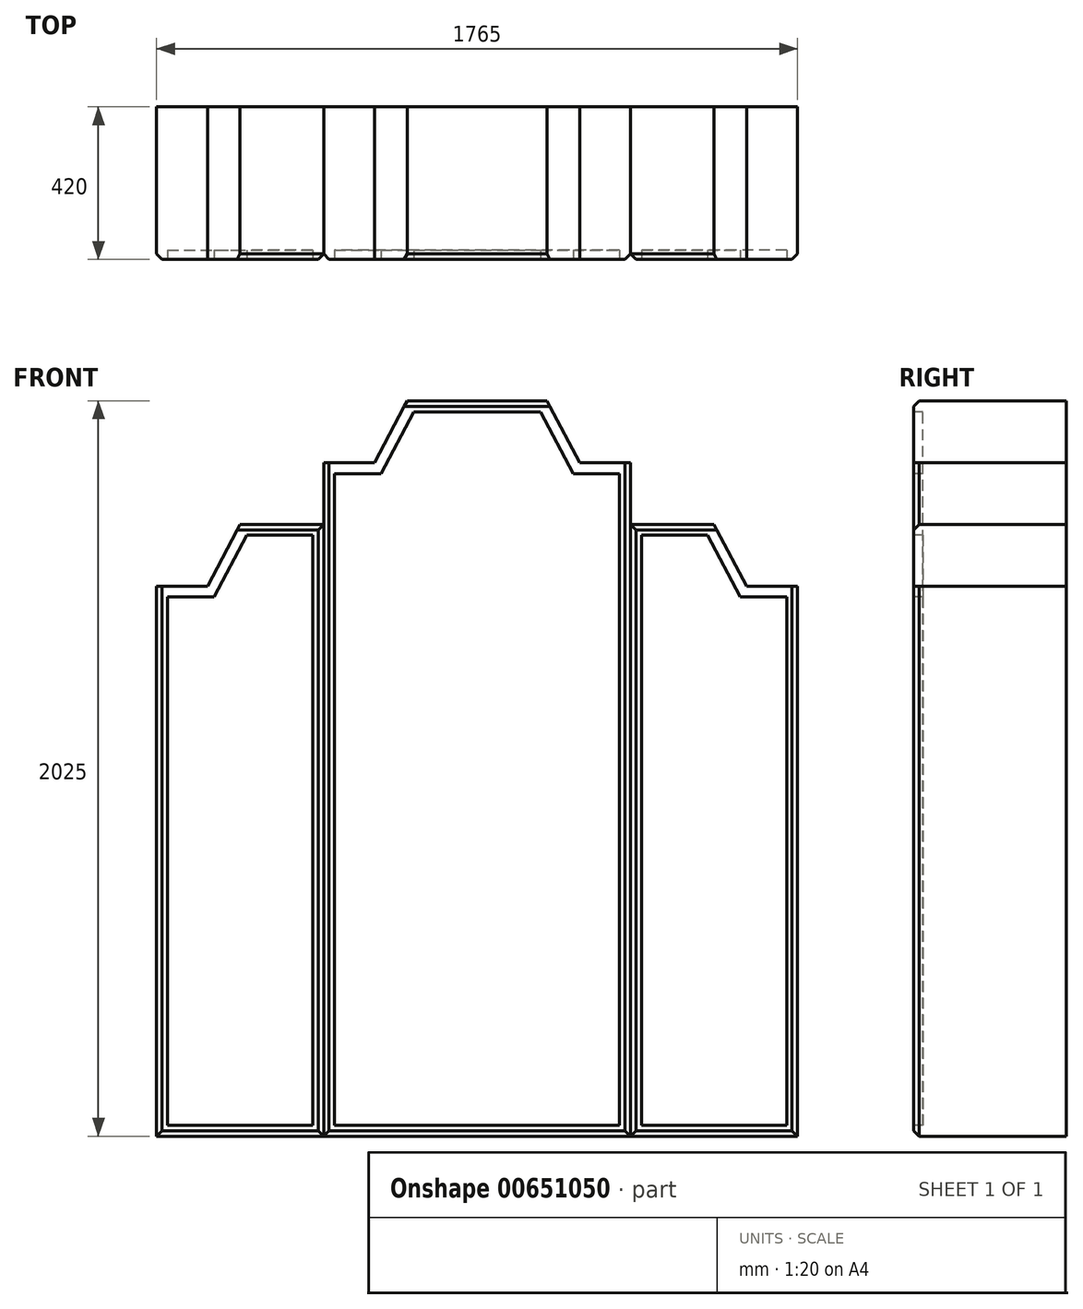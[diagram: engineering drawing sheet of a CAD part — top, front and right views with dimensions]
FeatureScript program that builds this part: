
annotation { "Feature Type Name" : "Feature", "Feature Type Description" : "" }
export const myFeature = defineFeature(function(context is Context, id is Id, definition is map)
    precondition{}
    {
        {
            var Q0;
            Q0=qCreatedBy(makeId("Top.planeOp"),FACE);
            var sketch = newSketch(context, id + "F0", { "sketchPlane" : qUnion([Q0])});
            skLineSegment(sketch, "E0.bottom", {"start": v(0, 0) * mm, "end": v(-460, 0) * mm});
            skLineSegment(sketch, "E0.top", {"start": v(0, 420) * mm, "end": v(-460, 420) * mm});
            skLineSegment(sketch, "E0.left", {"start": v(0, 0) * mm, "end": v(0, 420) * mm});
            skLineSegment(sketch, "E0.right", {"start": v(-460, 0) * mm, "end": v(-460, 420) * mm});
            skLineSegment(sketch, "E1.bottom", {"start": v(-460, 0) * mm, "end": v(-1305, 0) * mm});
            skLineSegment(sketch, "E1.top", {"start": v(-460, 420) * mm, "end": v(-1305, 420) * mm});
            skLineSegment(sketch, "E1.right", {"start": v(-1305, 0) * mm, "end": v(-1305, 420) * mm});
            skLineSegment(sketch, "E2.bottom", {"start": v(-1305, 0) * mm, "end": v(-1765, 0) * mm});
            skLineSegment(sketch, "E2.top", {"start": v(-1305, 420) * mm, "end": v(-1765, 420) * mm});
            skLineSegment(sketch, "E2.right", {"start": v(-1765, 0) * mm, "end": v(-1765, 420) * mm});
            skSolve(sketch);
        }
        {
            var Q0;
            Q0=makeQuery(id+"F0.imprint","IMPRINT",FACE,{"disambiguationData":[TD([[makeQuery(id+"F0.imprint","IMPRINT",EDGE,{"derivedFrom":sQuery(id+"F0.wireOp",EDGE,"E2.bottom")}),-1.0]])]});
            var Q1;
            Q1=makeQuery(id+"F0.imprint","IMPRINT",FACE,{"disambiguationData":[TD([[makeQuery(id+"F0.imprint","IMPRINT",EDGE,{"derivedFrom":sQuery(id+"F0.wireOp",EDGE,"E0.bottom")}),-1.0]])]});
            extrude(context, id + "F1", {"entities" : qUnion([Q0, Q1]), "depth" : 1685 * mm, "offsetDistance" : 25 * mm});
        }
        {
            var Q0;
            Q0=makeQuery(id+"F0.imprint","IMPRINT",FACE,{"disambiguationData":[TD([[makeQuery(id+"F0.imprint","IMPRINT",EDGE,{"derivedFrom":sQuery(id+"F0.wireOp",EDGE,"E1.bottom")}),-1.0]])]});
            extrude(context, id + "F2", {"entities" : qUnion([Q0]), "depth" : 2025 * mm, "offsetDistance" : 25 * mm});
        }
        {
            var Q0;
            Q0=makeQuery(id+"F1.opExtrude","SWEPT_FACE",FACE,{"disambiguationData":[OSD([sQuery(id+"F0.wireOp",EDGE,"E2.bottom")])]});
            var sketch = newSketch(context, id + "F3", { "sketchPlane" : qUnion([Q0])});
            skLineSegment(sketch, "E3.0.0", {"start": v(-1765, 0) * mm, "end": v(-1305, 0) * mm});
            skLineSegment(sketch, "E3.0.1", {"start": v(-1305, 0) * mm, "end": v(-1305, 1685) * mm});
            skLineSegment(sketch, "E3.0.2", {"start": v(-1305, 1685) * mm, "end": v(-1765, 1685) * mm});
            skLineSegment(sketch, "E3.0.3", {"start": v(-1765, 1685) * mm, "end": v(-1765, 0) * mm});
            skLineSegment(sketch, "E4.0.0", {"start": v(-1305, 0) * mm, "end": v(-460, 0) * mm});
            skLineSegment(sketch, "E4.0.1", {"start": v(-460, 0) * mm, "end": v(-460, 2025) * mm});
            skLineSegment(sketch, "E4.0.2", {"start": v(-460, 2025) * mm, "end": v(-1305, 2025) * mm});
            skLineSegment(sketch, "E4.0.3", {"start": v(-1305, 2025) * mm, "end": v(-1305, 0) * mm});
            skLineSegment(sketch, "E5.0.0", {"start": v(-460, 0) * mm, "end": v(0, 0) * mm});
            skLineSegment(sketch, "E5.0.1", {"start": v(0, 0) * mm, "end": v(0, 1685) * mm});
            skLineSegment(sketch, "E5.0.2", {"start": v(0, 1685) * mm, "end": v(-460, 1685) * mm});
            skLineSegment(sketch, "E5.0.3", {"start": v(-460, 1685) * mm, "end": v(-460, 0) * mm});
            skLineSegment(sketch, "E6", {"start": v(-1765, 1515) * mm, "end": v(-1625, 1515) * mm});
            skLineSegment(sketch, "E7", {"start": v(-1625, 1515) * mm, "end": v(-1535, 1685) * mm});
            skLineSegment(sketch, "E8", {"start": v(-1305, 1855) * mm, "end": v(-1165, 1855) * mm});
            skLineSegment(sketch, "E9", {"start": v(-1165, 1855) * mm, "end": v(-1075, 2025) * mm});
            skLineSegment(sketch, "E10", {"start": v(-882.5, 2375.74) * mm, "end": v(-882.5, -275.69) * mm, "construction": true});
            skPoint(sketch, "E10.startSnap0", {"position": v(-882.5, 2025) * mm});
            skLineSegment(sketch, "E11.MirrorCS", {"start": v(-600, 1855) * mm, "end": v(-690, 2025) * mm});
            skLineSegment(sketch, "E12.MirrorCS", {"start": v(-460, 1855) * mm, "end": v(-600, 1855) * mm});
            skLineSegment(sketch, "E13.MirrorCS", {"start": v(0, 1515) * mm, "end": v(-140, 1515) * mm});
            skLineSegment(sketch, "E14.MirrorCS", {"start": v(-140, 1515) * mm, "end": v(-230, 1685) * mm});
            skSolve(sketch);
        }
        {
            var Q0;
            {var subQ4=sQuery(id+"F3.wireOp",EDGE,"E6");Q0=makeQuery(id+"F3.imprint","IMPRINT",FACE,{"disambiguationData":[TD([[makeQuery(id+"F3.imprint","IMPRINT",EDGE,{"derivedFrom":subQ4}),1.0]])]});}
            var Q1;
            {var subQ4=sQuery(id+"F3.wireOp",EDGE,"E11.MirrorCS");Q1=makeQuery(id+"F3.imprint","IMPRINT",FACE,{"disambiguationData":[TD([[makeQuery(id+"F3.imprint","IMPRINT",EDGE,{"derivedFrom":subQ4}),-1.0]])]});}
            var Q2;
            {var subQ4=sQuery(id+"F3.wireOp",EDGE,"E8");Q2=makeQuery(id+"F3.imprint","IMPRINT",FACE,{"disambiguationData":[TD([[makeQuery(id+"F3.imprint","IMPRINT",EDGE,{"derivedFrom":subQ4}),1.0]])]});}
            var Q3;
            {var subQ3=sQuery(id+"F3.wireOp",EDGE,"E13.MirrorCS");Q3=makeQuery(id+"F3.imprint","IMPRINT",FACE,{"disambiguationData":[TD([[makeQuery(id+"F3.imprint","IMPRINT",EDGE,{"derivedFrom":subQ3}),-1.0]])]});}
            extrude(context, id + "F4", {"entities" : qUnion([Q0, Q1, Q2, Q3]), "operationType" : NewBodyOperationType.REMOVE, "oppositeDirection" : true, "depth" : 420 * mm, "offsetDistance" : 25 * mm});
        }
        {
            var Q0;
            Q0=makeQuery(id+"F2.opExtrude","SWEPT_FACE",FACE,{"disambiguationData":[OSD([sQuery(id+"F0.wireOp",EDGE,"E1.bottom")])]});
            var sketch = newSketch(context, id + "F5", { "sketchPlane" : qUnion([Q0])});
            skLineSegment(sketch, "E15.0.0", {"start": v(-1625, 1515) * mm, "end": v(-1765, 1515) * mm});
            skLineSegment(sketch, "E15.0.1", {"start": v(-1765, 1515) * mm, "end": v(-1765, 0) * mm});
            skLineSegment(sketch, "E15.0.2", {"start": v(-1765, 0) * mm, "end": v(-1305, 0) * mm});
            skLineSegment(sketch, "E15.0.3", {"start": v(-1305, 0) * mm, "end": v(-1305, 1685) * mm});
            skLineSegment(sketch, "E15.0.4", {"start": v(-1305, 1685) * mm, "end": v(-1535, 1685) * mm});
            skLineSegment(sketch, "E15.0.5", {"start": v(-1535, 1685) * mm, "end": v(-1625, 1515) * mm});
            skLineSegment(sketch, "E16.0.0", {"start": v(-460, 0) * mm, "end": v(-460, 1855) * mm});
            skLineSegment(sketch, "E16.0.1", {"start": v(-460, 1855) * mm, "end": v(-600, 1855) * mm});
            skLineSegment(sketch, "E16.0.2", {"start": v(-600, 1855) * mm, "end": v(-690, 2025) * mm});
            skLineSegment(sketch, "E16.0.3", {"start": v(-690, 2025) * mm, "end": v(-1075, 2025) * mm});
            skLineSegment(sketch, "E16.0.4", {"start": v(-1075, 2025) * mm, "end": v(-1165, 1855) * mm});
            skLineSegment(sketch, "E16.0.5", {"start": v(-1165, 1855) * mm, "end": v(-1305, 1855) * mm});
            skLineSegment(sketch, "E16.0.6", {"start": v(-1305, 1855) * mm, "end": v(-1305, 0) * mm});
            skLineSegment(sketch, "E16.0.7", {"start": v(-1305, 0) * mm, "end": v(-460, 0) * mm});
            skLineSegment(sketch, "E17.0.0", {"start": v(0, 1515) * mm, "end": v(-140, 1515) * mm});
            skLineSegment(sketch, "E17.0.1", {"start": v(-140, 1515) * mm, "end": v(-230, 1685) * mm});
            skLineSegment(sketch, "E17.0.2", {"start": v(-230, 1685) * mm, "end": v(-460, 1685) * mm});
            skLineSegment(sketch, "E17.0.3", {"start": v(-460, 1685) * mm, "end": v(-460, 0) * mm});
            skLineSegment(sketch, "E17.0.4", {"start": v(-460, 0) * mm, "end": v(0, 0) * mm});
            skLineSegment(sketch, "E17.0.5", {"start": v(0, 0) * mm, "end": v(0, 1515) * mm});
            skLineSegment(sketch, "E18.bottom", {"start": v(-1735, 1485) * mm, "end": v(-1606.94, 1485) * mm});
            skLineSegment(sketch, "E18.top", {"start": v(-1735, 30) * mm, "end": v(-1335, 30) * mm});
            skLineSegment(sketch, "E18.left", {"start": v(-1735, 1485) * mm, "end": v(-1735, 30) * mm});
            skLineSegment(sketch, "E18.right", {"start": v(-1335, 1485) * mm, "end": v(-1335, 30) * mm});
            skLineSegment(sketch, "E19.bottom", {"start": v(-30, 1485) * mm, "end": v(-158.06, 1485) * mm});
            skLineSegment(sketch, "E19.top", {"start": v(-30, 30) * mm, "end": v(-430, 30) * mm});
            skLineSegment(sketch, "E19.left", {"start": v(-30, 1485) * mm, "end": v(-30, 30) * mm});
            skLineSegment(sketch, "E19.right", {"start": v(-430, 1485) * mm, "end": v(-430, 30) * mm});
            skLineSegment(sketch, "E20", {"start": v(-1056.94, 1995) * mm, "end": v(-708.06, 1995) * mm});
            skLineSegment(sketch, "E21", {"start": v(-708.06, 1995) * mm, "end": v(-618.06, 1825) * mm});
            skLineSegment(sketch, "E22", {"start": v(-618.06, 1825) * mm, "end": v(-490, 1825) * mm});
            skLineSegment(sketch, "E23", {"start": v(-490, 1825) * mm, "end": v(-490, 30) * mm});
            skLineSegment(sketch, "E24", {"start": v(-490, 30) * mm, "end": v(-1275, 30) * mm});
            skLineSegment(sketch, "E25", {"start": v(-1275, 30) * mm, "end": v(-1275, 1825) * mm});
            skLineSegment(sketch, "E26", {"start": v(-1275, 1825) * mm, "end": v(-1146.94, 1825) * mm});
            skLineSegment(sketch, "E27", {"start": v(-1146.94, 1825) * mm, "end": v(-1056.94, 1995) * mm});
            skLineSegment(sketch, "E28", {"start": v(-1606.94, 1485) * mm, "end": v(-1516.94, 1655) * mm});
            skLineSegment(sketch, "E29", {"start": v(-1335, 1485) * mm, "end": v(-1335, 1655) * mm});
            skLineSegment(sketch, "E30", {"start": v(-1335, 1655) * mm, "end": v(-1516.94, 1655) * mm});
            skLineSegment(sketch, "E31", {"start": v(-430, 1485) * mm, "end": v(-430, 1655) * mm});
            skLineSegment(sketch, "E32", {"start": v(-430, 1655) * mm, "end": v(-248.06, 1655) * mm});
            skLineSegment(sketch, "E33", {"start": v(-248.06, 1655) * mm, "end": v(-158.06, 1485) * mm});
            skSolve(sketch);
        }
        {
            var Q0;
            Q0=makeQuery(id+"F5.imprint","IMPRINT",FACE,{"disambiguationData":[TD([[makeQuery(id+"F5.imprint","IMPRINT",EDGE,{"derivedFrom":sQuery(id+"F5.wireOp",EDGE,"E20")}),-1.0]])]});
            var Q1;
            Q1=makeQuery(id+"F5.imprint","IMPRINT",FACE,{"disambiguationData":[TD([[makeQuery(id+"F5.imprint","IMPRINT",EDGE,{"derivedFrom":sQuery(id+"F5.wireOp",EDGE,"E18.bottom")}),-1.0]])]});
            var Q2;
            Q2=makeQuery(id+"F5.imprint","IMPRINT",FACE,{"disambiguationData":[TD([[makeQuery(id+"F5.imprint","IMPRINT",EDGE,{"derivedFrom":sQuery(id+"F5.wireOp",EDGE,"E19.bottom")}),1.0]])]});
            extrude(context, id + "F6", {"entities" : qUnion([Q0, Q1, Q2]), "operationType" : NewBodyOperationType.REMOVE, "oppositeDirection" : true, "depth" : 25 * mm, "offsetDistance" : 25 * mm});
        }
        {
            var Q0;
            Q0=makeQuery(id+"F1.opExtrude","SWEPT_EDGE",EDGE,{"disambiguationData":[OSD([sQuery(id+"F0.wireOp",EDGE,"E0.bottom"),sQuery(id+"F0.wireOp",EDGE,"E0.left")])]});
            var Q1;
            Q1=makeQuery(id+"F6.boolean.opBoolean","COPY",EDGE,{"derivedFrom":makeQuery(id+"F6.opExtrude","CAP_EDGE",EDGE,{"disambiguationData":[OSD([sQuery(id+"F5.wireOp",EDGE,"E19.left")])],"isStart":true})});
            var Q2;
            Q2=makeQuery(id+"F6.boolean.opBoolean","COPY",EDGE,{"derivedFrom":makeQuery(id+"F6.opExtrude","CAP_EDGE",EDGE,{"disambiguationData":[OSD([sQuery(id+"F5.wireOp",EDGE,"E19.bottom")])],"isStart":true})});
            var Q3;
            Q3=makeQuery(id+"F4.boolean.opBoolean","COPY",EDGE,{"derivedFrom":makeQuery(id+"F4.opExtrude","CAP_EDGE",EDGE,{"disambiguationData":[OSD([sQuery(id+"F3.wireOp",EDGE,"E13.MirrorCS")])],"isStart":true})});
            var Q4;
            Q4=makeQuery(id+"F6.boolean.opBoolean","COPY",EDGE,{"derivedFrom":makeQuery(id+"F6.opExtrude","CAP_EDGE",EDGE,{"disambiguationData":[OSD([sQuery(id+"F5.wireOp",EDGE,"E33")])],"isStart":true})});
            var Q5;
            Q5=makeQuery(id+"F4.boolean.opBoolean","COPY",EDGE,{"derivedFrom":makeQuery(id+"F4.opExtrude","CAP_EDGE",EDGE,{"disambiguationData":[OSD([sQuery(id+"F3.wireOp",EDGE,"E14.MirrorCS")])],"isStart":true})});
            var Q6;
            Q6=makeQuery(id+"F6.boolean.opBoolean","COPY",EDGE,{"derivedFrom":makeQuery(id+"F6.opExtrude","CAP_EDGE",EDGE,{"disambiguationData":[OSD([sQuery(id+"F5.wireOp",EDGE,"E32")])],"isStart":true})});
            var Q7;
            Q7=makeQuery(id+"F1.opExtrude","CAP_EDGE",EDGE,{"disambiguationData":[OSD([sQuery(id+"F0.wireOp",EDGE,"E0.bottom")])],"isStart":false});
            var Q8;
            Q8=makeQuery(id+"F6.boolean.opBoolean","COPY",EDGE,{"derivedFrom":makeQuery(id+"F6.opExtrude","CAP_EDGE",EDGE,{"disambiguationData":[OSD([sQuery(id+"F5.wireOp",EDGE,"E19.right"),sQuery(id+"F5.wireOp",EDGE,"E31")])],"isStart":true})});
            var Q9;
            Q9=makeQuery(id+"F1.opExtrude","SWEPT_EDGE",EDGE,{"disambiguationData":[OSD([sQuery(id+"F0.wireOp",EDGE,"E0.bottom"),sQuery(id+"F0.wireOp",EDGE,"E1.bottom"),sQuery(id+"F0.wireOp",EDGE,"E0.right")])]});
            var Q10;
            Q10=makeQuery(id+"F6.boolean.opBoolean","COPY",EDGE,{"derivedFrom":makeQuery(id+"F6.opExtrude","CAP_EDGE",EDGE,{"disambiguationData":[OSD([sQuery(id+"F5.wireOp",EDGE,"E19.top")])],"isStart":true})});
            var Q11;
            Q11=makeQuery(id+"F1.opExtrude","CAP_EDGE",EDGE,{"disambiguationData":[OSD([sQuery(id+"F0.wireOp",EDGE,"E0.bottom")])],"isStart":true});
            var Q12;
            Q12=makeQuery(id+"F1.opExtrude","SWEPT_EDGE",EDGE,{"disambiguationData":[OSD([sQuery(id+"F0.wireOp",EDGE,"E2.bottom"),sQuery(id+"F0.wireOp",EDGE,"E2.right")])]});
            var Q13;
            Q13=makeQuery(id+"F6.boolean.opBoolean","COPY",EDGE,{"derivedFrom":makeQuery(id+"F6.opExtrude","CAP_EDGE",EDGE,{"disambiguationData":[OSD([sQuery(id+"F5.wireOp",EDGE,"E18.left")])],"isStart":true})});
            var Q14;
            Q14=makeQuery(id+"F6.boolean.opBoolean","COPY",EDGE,{"derivedFrom":makeQuery(id+"F6.opExtrude","CAP_EDGE",EDGE,{"disambiguationData":[OSD([sQuery(id+"F5.wireOp",EDGE,"E18.bottom")])],"isStart":true})});
            var Q15;
            Q15=makeQuery(id+"F6.boolean.opBoolean","COPY",EDGE,{"derivedFrom":makeQuery(id+"F6.opExtrude","CAP_EDGE",EDGE,{"disambiguationData":[OSD([sQuery(id+"F5.wireOp",EDGE,"E28")])],"isStart":true})});
            var Q16;
            Q16=makeQuery(id+"F6.boolean.opBoolean","COPY",EDGE,{"derivedFrom":makeQuery(id+"F6.opExtrude","CAP_EDGE",EDGE,{"disambiguationData":[OSD([sQuery(id+"F5.wireOp",EDGE,"E30")])],"isStart":true})});
            var Q17;
            Q17=makeQuery(id+"F1.opExtrude","CAP_EDGE",EDGE,{"disambiguationData":[OSD([sQuery(id+"F0.wireOp",EDGE,"E2.bottom")])],"isStart":false});
            var Q18;
            Q18=makeQuery(id+"F4.boolean.opBoolean","COPY",EDGE,{"derivedFrom":makeQuery(id+"F4.opExtrude","CAP_EDGE",EDGE,{"disambiguationData":[OSD([sQuery(id+"F3.wireOp",EDGE,"E7")])],"isStart":true})});
            var Q19;
            Q19=makeQuery(id+"F4.boolean.opBoolean","COPY",EDGE,{"derivedFrom":makeQuery(id+"F4.opExtrude","CAP_EDGE",EDGE,{"disambiguationData":[OSD([sQuery(id+"F3.wireOp",EDGE,"E6")])],"isStart":true})});
            var Q20;
            Q20=makeQuery(id+"F6.boolean.opBoolean","COPY",EDGE,{"derivedFrom":makeQuery(id+"F6.opExtrude","CAP_EDGE",EDGE,{"disambiguationData":[OSD([sQuery(id+"F5.wireOp",EDGE,"E18.right"),sQuery(id+"F5.wireOp",EDGE,"E29")])],"isStart":true})});
            var Q21;
            Q21=makeQuery(id+"F6.boolean.opBoolean","COPY",EDGE,{"derivedFrom":makeQuery(id+"F6.opExtrude","CAP_EDGE",EDGE,{"disambiguationData":[OSD([sQuery(id+"F5.wireOp",EDGE,"E18.top")])],"isStart":true})});
            var Q22;
            Q22=makeQuery(id+"F1.opExtrude","CAP_EDGE",EDGE,{"disambiguationData":[OSD([sQuery(id+"F0.wireOp",EDGE,"E2.bottom")])],"isStart":true});
            var Q23;
            Q23=makeQuery(id+"F1.opExtrude","SWEPT_EDGE",EDGE,{"disambiguationData":[OSD([sQuery(id+"F0.wireOp",EDGE,"E1.bottom"),sQuery(id+"F0.wireOp",EDGE,"E2.bottom"),sQuery(id+"F0.wireOp",EDGE,"E1.right")])]});
            var Q24;
            Q24=makeQuery(id+"F2.opExtrude","SWEPT_EDGE",EDGE,{"disambiguationData":[OSD([sQuery(id+"F0.wireOp",EDGE,"E1.bottom"),sQuery(id+"F0.wireOp",EDGE,"E2.bottom"),sQuery(id+"F0.wireOp",EDGE,"E1.right")])]});
            var Q25;
            Q25=makeQuery(id+"F6.boolean.opBoolean","COPY",EDGE,{"derivedFrom":makeQuery(id+"F6.opExtrude","CAP_EDGE",EDGE,{"disambiguationData":[OSD([sQuery(id+"F5.wireOp",EDGE,"E25")])],"isStart":true})});
            var Q26;
            Q26=makeQuery(id+"F6.boolean.opBoolean","COPY",EDGE,{"derivedFrom":makeQuery(id+"F6.opExtrude","CAP_EDGE",EDGE,{"disambiguationData":[OSD([sQuery(id+"F5.wireOp",EDGE,"E26")])],"isStart":true})});
            var Q27;
            Q27=makeQuery(id+"F4.boolean.opBoolean","COPY",EDGE,{"derivedFrom":makeQuery(id+"F4.opExtrude","CAP_EDGE",EDGE,{"disambiguationData":[OSD([sQuery(id+"F3.wireOp",EDGE,"E8")])],"isStart":true})});
            var Q28;
            Q28=makeQuery(id+"F4.boolean.opBoolean","COPY",EDGE,{"derivedFrom":makeQuery(id+"F4.opExtrude","CAP_EDGE",EDGE,{"disambiguationData":[OSD([sQuery(id+"F3.wireOp",EDGE,"E9")])],"isStart":true})});
            var Q29;
            Q29=makeQuery(id+"F6.boolean.opBoolean","COPY",EDGE,{"derivedFrom":makeQuery(id+"F6.opExtrude","CAP_EDGE",EDGE,{"disambiguationData":[OSD([sQuery(id+"F5.wireOp",EDGE,"E27")])],"isStart":true})});
            var Q30;
            Q30=makeQuery(id+"F6.boolean.opBoolean","COPY",EDGE,{"derivedFrom":makeQuery(id+"F6.opExtrude","CAP_EDGE",EDGE,{"disambiguationData":[OSD([sQuery(id+"F5.wireOp",EDGE,"E20")])],"isStart":true})});
            var Q31;
            Q31=makeQuery(id+"F2.opExtrude","CAP_EDGE",EDGE,{"disambiguationData":[OSD([sQuery(id+"F0.wireOp",EDGE,"E1.bottom")])],"isStart":false});
            var Q32;
            Q32=makeQuery(id+"F4.boolean.opBoolean","COPY",EDGE,{"derivedFrom":makeQuery(id+"F4.opExtrude","CAP_EDGE",EDGE,{"disambiguationData":[OSD([sQuery(id+"F3.wireOp",EDGE,"E11.MirrorCS")])],"isStart":true})});
            var Q33;
            Q33=makeQuery(id+"F6.boolean.opBoolean","COPY",EDGE,{"derivedFrom":makeQuery(id+"F6.opExtrude","CAP_EDGE",EDGE,{"disambiguationData":[OSD([sQuery(id+"F5.wireOp",EDGE,"E21")])],"isStart":true})});
            var Q34;
            Q34=makeQuery(id+"F6.boolean.opBoolean","COPY",EDGE,{"derivedFrom":makeQuery(id+"F6.opExtrude","CAP_EDGE",EDGE,{"disambiguationData":[OSD([sQuery(id+"F5.wireOp",EDGE,"E22")])],"isStart":true})});
            var Q35;
            Q35=makeQuery(id+"F4.boolean.opBoolean","COPY",EDGE,{"derivedFrom":makeQuery(id+"F4.opExtrude","CAP_EDGE",EDGE,{"disambiguationData":[OSD([sQuery(id+"F3.wireOp",EDGE,"E12.MirrorCS")])],"isStart":true})});
            var Q36;
            Q36=makeQuery(id+"F6.boolean.opBoolean","COPY",EDGE,{"derivedFrom":makeQuery(id+"F6.opExtrude","CAP_EDGE",EDGE,{"disambiguationData":[OSD([sQuery(id+"F5.wireOp",EDGE,"E23")])],"isStart":true})});
            var Q37;
            Q37=makeQuery(id+"F2.opExtrude","SWEPT_EDGE",EDGE,{"disambiguationData":[OSD([sQuery(id+"F0.wireOp",EDGE,"E0.bottom"),sQuery(id+"F0.wireOp",EDGE,"E1.bottom"),sQuery(id+"F0.wireOp",EDGE,"E0.right")])]});
            var Q38;
            Q38=makeQuery(id+"F6.boolean.opBoolean","COPY",EDGE,{"derivedFrom":makeQuery(id+"F6.opExtrude","CAP_EDGE",EDGE,{"disambiguationData":[OSD([sQuery(id+"F5.wireOp",EDGE,"E24")])],"isStart":true})});
            var Q39;
            Q39=makeQuery(id+"F2.opExtrude","CAP_EDGE",EDGE,{"disambiguationData":[OSD([sQuery(id+"F0.wireOp",EDGE,"E1.bottom")])],"isStart":true});
            chamfer(context, id + "F7", {"entities" : qUnion([Q0, Q1, Q2, Q3, Q4, Q5, Q6, Q7, Q8, Q9, Q10, Q11, Q12, Q13, Q14, Q15, Q16, Q17, Q18, Q19, Q20, Q21, Q22, Q23, Q24, Q25, Q26, Q27, Q28, Q29, Q30, Q31, Q32, Q33, Q34, Q35, Q36, Q37, Q38, Q39]), "width" : 15 * mm, "tangentPropagation" : true});
        }
    });
